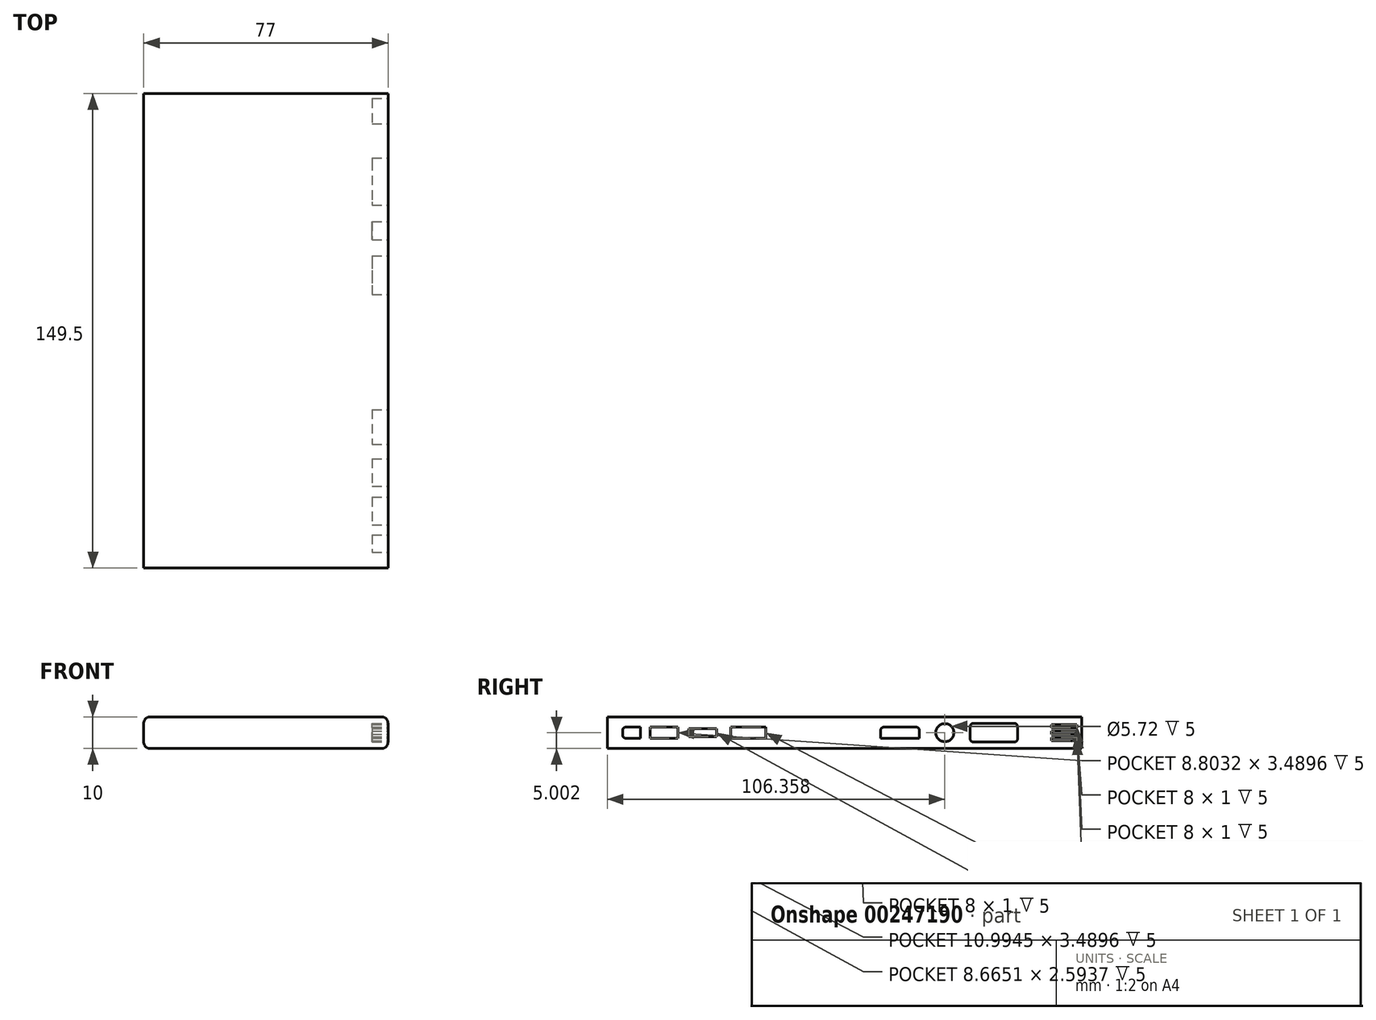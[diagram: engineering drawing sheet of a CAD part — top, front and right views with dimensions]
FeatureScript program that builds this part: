
annotation { "Feature Type Name" : "Feature", "Feature Type Description" : "" }
export const myFeature = defineFeature(function(context is Context, id is Id, definition is map)
    precondition{}
    {
        {
            var Q0;
            Q0=qCreatedBy(makeId("Right.planeOp"),FACE);
            var sketch = newSketch(context, id + "F0", { "sketchPlane" : qUnion([Q0])});
            skLineSegment(sketch, "E0.bottom", {"start": v(-69.22, 6.6) * mm, "end": v(80.28, 6.6) * mm});
            skLineSegment(sketch, "E0.top", {"start": v(-69.22, 16.6) * mm, "end": v(80.28, 16.6) * mm});
            skLineSegment(sketch, "E0.left", {"start": v(-69.22, 6.6) * mm, "end": v(-69.22, 16.6) * mm});
            skLineSegment(sketch, "E0.right", {"start": v(80.28, 6.6) * mm, "end": v(80.28, 16.6) * mm});
            skSolve(sketch);
        }
        {
            var Q0;
            Q0 = qSketchRegion(id + "F0", true);
            extrude(context, id + "F1", {"entities" : qUnion([Q0]), "depth" : 77 * mm});
        }
        {
            var Q0;
            Q0=makeQuery(id+"F1.opExtrude","CAP_FACE",FACE,{"disambiguationData":[OSD([sQuery(id+"F0.wireOp",EDGE,"E0.bottom"),sQuery(id+"F0.wireOp",EDGE,"E0.top"),sQuery(id+"F0.wireOp",EDGE,"E0.left"),sQuery(id+"F0.wireOp",EDGE,"E0.right")])],"isStart":false});
            var sketch = newSketch(context, id + "F2", { "sketchPlane" : qUnion([Q0])});
            skLineSegment(sketch, "E1", {"start": v(-69.22, 11.6) * mm, "end": v(85.24, 11.6) * mm, "construction": true});
            skLineSegment(sketch, "E2.bottom", {"start": v(-46.93, 13.34) * mm, "end": v(-55.74, 13.34) * mm});
            skLineSegment(sketch, "E2.top", {"start": v(-46.93, 9.85) * mm, "end": v(-55.74, 9.85) * mm});
            skLineSegment(sketch, "E2.left", {"start": v(-46.93, 13.34) * mm, "end": v(-46.93, 9.85) * mm});
            skLineSegment(sketch, "E2.right", {"start": v(-55.74, 13.34) * mm, "end": v(-55.74, 9.85) * mm});
            skPoint(sketch, "E2.middle", {"position": v(-51.33, 11.6) * mm});
            skLineSegment(sketch, "E3.bottom", {"start": v(-34.82, 12.89) * mm, "end": v(-43.49, 12.89) * mm});
            skLineSegment(sketch, "E3.top", {"start": v(-34.82, 10.3) * mm, "end": v(-43.49, 10.3) * mm});
            skLineSegment(sketch, "E3.left", {"start": v(-34.82, 12.89) * mm, "end": v(-34.82, 10.3) * mm});
            skLineSegment(sketch, "E3.right", {"start": v(-43.49, 12.89) * mm, "end": v(-43.49, 10.3) * mm});
            skPoint(sketch, "E3.middle", {"position": v(-39.15, 11.6) * mm});
            skLineSegment(sketch, "E4.bottom", {"start": v(-19.3, 13.34) * mm, "end": v(-30.3, 13.34) * mm});
            skLineSegment(sketch, "E4.top", {"start": v(-19.3, 9.85) * mm, "end": v(-30.3, 9.85) * mm});
            skLineSegment(sketch, "E4.left", {"start": v(-19.3, 13.34) * mm, "end": v(-19.3, 9.85) * mm});
            skLineSegment(sketch, "E4.right", {"start": v(-30.3, 13.34) * mm, "end": v(-30.3, 9.85) * mm});
            skPoint(sketch, "E4.middle", {"position": v(-24.8, 11.6) * mm});
            skLineSegment(sketch, "E5.bottom", {"start": v(28.14, 13.34) * mm, "end": v(17.92, 13.34) * mm});
            skLineSegment(sketch, "E5.top", {"start": v(29.14, 9.85) * mm, "end": v(16.92, 9.85) * mm});
            skLineSegment(sketch, "E5.left", {"start": v(29.14, 12.34) * mm, "end": v(29.14, 9.85) * mm});
            skLineSegment(sketch, "E5.right", {"start": v(16.92, 12.34) * mm, "end": v(16.92, 9.85) * mm});
            skPoint(sketch, "E5.middle", {"position": v(23.03, 11.6) * mm});
            skLineSegment(sketch, "E6.bottom", {"start": v(59.06, 14.55) * mm, "end": v(46.14, 14.55) * mm});
            skLineSegment(sketch, "E6.top", {"start": v(59.06, 8.63) * mm, "end": v(46.14, 8.63) * mm});
            skLineSegment(sketch, "E6.left", {"start": v(60.06, 13.55) * mm, "end": v(60.06, 9.63) * mm});
            skLineSegment(sketch, "E6.right", {"start": v(45.14, 13.55) * mm, "end": v(45.14, 9.63) * mm});
            skPoint(sketch, "E6.middle", {"position": v(52.6, 11.6) * mm});
            skLineSegment(sketch, "E7.bottom", {"start": v(78.75, 12.1) * mm, "end": v(70.75, 12.1) * mm});
            skLineSegment(sketch, "E7.top", {"start": v(78.75, 11.1) * mm, "end": v(70.75, 11.1) * mm});
            skLineSegment(sketch, "E7.left", {"start": v(78.75, 12.1) * mm, "end": v(78.75, 11.1) * mm});
            skLineSegment(sketch, "E7.right", {"start": v(70.75, 12.1) * mm, "end": v(70.75, 11.1) * mm});
            skPoint(sketch, "E7.middle", {"position": v(74.75, 11.6) * mm});
            skCircle(sketch, "E8", {"center": v(37.14, 11.6) * mm, "radius": 2.86 * mm});
            skLineSegment(sketch, "E9.bottom", {"start": v(78.75, 13.1) * mm, "end": v(70.75, 13.1) * mm});
            skLineSegment(sketch, "E9.top", {"start": v(78.75, 14.1) * mm, "end": v(70.75, 14.1) * mm});
            skLineSegment(sketch, "E9.left", {"start": v(78.75, 13.1) * mm, "end": v(78.75, 14.1) * mm});
            skLineSegment(sketch, "E9.right", {"start": v(70.75, 13.1) * mm, "end": v(70.75, 14.1) * mm});
            skPoint(sketch, "E9.middle", {"position": v(74.75, 13.6) * mm});
            skPoint(sketch, "E9.middle.positionSnap0", {"position": v(74.75, 12.1) * mm});
            skPoint(sketch, "E9.centerSnap0", {"position": v(74.75, 12.1) * mm});
            skLineSegment(sketch, "E10.bottom", {"start": v(78.75, 10.1) * mm, "end": v(70.75, 10.1) * mm});
            skLineSegment(sketch, "E10.top", {"start": v(78.75, 9.1) * mm, "end": v(70.75, 9.1) * mm});
            skLineSegment(sketch, "E10.left", {"start": v(78.75, 10.1) * mm, "end": v(78.75, 9.1) * mm});
            skLineSegment(sketch, "E10.right", {"start": v(70.75, 10.1) * mm, "end": v(70.75, 9.1) * mm});
            skPoint(sketch, "E10.middle", {"position": v(74.75, 9.6) * mm});
            skPoint(sketch, "E11.visualSharp", {"position": v(45.14, 14.55) * mm});
            skArc(sketch, "E11.filletArc", {"start": v(46.14, 14.55) * mm, "mid": v(45.43, 14.26) * mm, "end": v(45.14, 13.55) * mm});
            skPoint(sketch, "E12.visualSharp", {"position": v(60.06, 14.55) * mm});
            skArc(sketch, "E12.filletArc", {"start": v(60.06, 13.55) * mm, "mid": v(59.77, 14.26) * mm, "end": v(59.06, 14.55) * mm});
            skPoint(sketch, "E13.visualSharp", {"position": v(60.06, 8.63) * mm});
            skArc(sketch, "E13.filletArc", {"start": v(59.06, 8.63) * mm, "mid": v(59.77, 8.92) * mm, "end": v(60.06, 9.63) * mm});
            skPoint(sketch, "E14.visualSharp", {"position": v(45.14, 8.63) * mm});
            skArc(sketch, "E14.filletArc", {"start": v(45.14, 9.63) * mm, "mid": v(45.43, 8.92) * mm, "end": v(46.14, 8.63) * mm});
            skPoint(sketch, "E15.visualSharp", {"position": v(16.92, 13.34) * mm});
            skArc(sketch, "E15.filletArc", {"start": v(17.92, 13.34) * mm, "mid": v(17.21, 13.04) * mm, "end": v(16.92, 12.34) * mm});
            skPoint(sketch, "E16.visualSharp", {"position": v(29.14, 13.34) * mm});
            skArc(sketch, "E16.filletArc", {"start": v(29.14, 12.34) * mm, "mid": v(28.85, 13.04) * mm, "end": v(28.14, 13.34) * mm});
            skLineSegment(sketch, "E17.bottom", {"start": v(-58.82, 13.38) * mm, "end": v(-63.36, 13.38) * mm});
            skLineSegment(sketch, "E17.top", {"start": v(-58.82, 9.8) * mm, "end": v(-63.36, 9.8) * mm});
            skLineSegment(sketch, "E17.left", {"start": v(-58.82, 13.38) * mm, "end": v(-58.82, 9.8) * mm});
            skLineSegment(sketch, "E17.right", {"start": v(-64.36, 12.38) * mm, "end": v(-64.36, 10.8) * mm});
            skPoint(sketch, "E17.middle", {"position": v(-61.59, 11.6) * mm});
            skPoint(sketch, "E18.visualSharp", {"position": v(-64.36, 13.38) * mm});
            skArc(sketch, "E18.filletArc", {"start": v(-63.36, 13.38) * mm, "mid": v(-64.06, 13.09) * mm, "end": v(-64.36, 12.38) * mm});
            skPoint(sketch, "E19.visualSharp", {"position": v(-64.36, 9.8) * mm});
            skArc(sketch, "E19.filletArc", {"start": v(-64.36, 10.8) * mm, "mid": v(-64.06, 10.1) * mm, "end": v(-63.36, 9.8) * mm});
            skSolve(sketch);
        }
        {
            var Q0;
            Q0 = qSketchRegion(id + "F2", true);
            extrude(context, id + "F3", {"entities" : qUnion([Q0]), "operationType" : NewBodyOperationType.REMOVE, "oppositeDirection" : true, "depth" : 5 * mm});
        }
        {
            var Q0;
            Q0=makeQuery(id+"F1.opExtrude","CAP_EDGE",EDGE,{"disambiguationData":[OSD([sQuery(id+"F0.wireOp",EDGE,"E0.top")])],"isStart":false});
            var Q1;
            Q1=makeQuery(id+"F1.opExtrude","CAP_EDGE",EDGE,{"disambiguationData":[OSD([sQuery(id+"F0.wireOp",EDGE,"E0.bottom")])],"isStart":false});
            var Q2;
            Q2=makeQuery(id+"F1.opExtrude","CAP_EDGE",EDGE,{"disambiguationData":[OSD([sQuery(id+"F0.wireOp",EDGE,"E0.top")])],"isStart":true});
            var Q3;
            Q3=makeQuery(id+"F1.opExtrude","CAP_EDGE",EDGE,{"disambiguationData":[OSD([sQuery(id+"F0.wireOp",EDGE,"E0.bottom")])],"isStart":true});
            fillet(context, id + "F4", {"entities" : qUnion([Q0, Q1, Q2, Q3]), "radius" : 2 * mm, "tangentPropagation" : true, "allowEdgeOverflow" : false});
        }
    });
